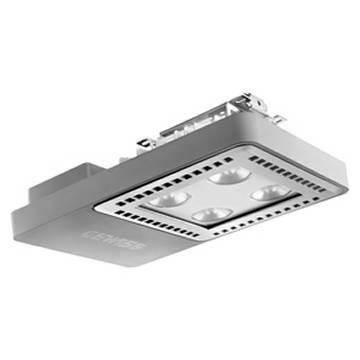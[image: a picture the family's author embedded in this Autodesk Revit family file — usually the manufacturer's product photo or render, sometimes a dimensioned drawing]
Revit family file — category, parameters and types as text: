
# Revit family: Lighting-Industrial-GEWISS-SMART[4]HE_HIGHBAYS-LED_EMERGENCY_1M
name_source: partatom
category: Apparecchi per illuminazione
units: mm (PartAtom-declared; Revit-internal decimal feet)

## family parameters
Basato su piano di lavoro = Sì
Condiviso = No
Numero OmniClass = 23.80.70.00
Punto di calcolo locali = No
Quota connettore circolare = Usa diametro
Sempre verticale = No
Sorgente d'illuminazione = No
Taglio con vuoti quando caricato = No
Tipo di parte = Normale
Titolo OmniClass = Lighting

## types (18) — shared parameters
Application = Internal
Batteria = <Per categoria>
Body = PA6 "Halogen Free" loaded fibreglass
Carico apparente = 53 VA
Catalogue = LIGHTING
Classification: = -
Classificazione = Lighting
Color Rendering Index = CRI-80
Colour = Grey RAL 7035
Colour : = Grey RAL 7035
Context = Logistics and industrial manufacturing lighting
Control System = 1 x DALI DT6 + 1 x DALI DT1 (Emerg. 3h)
DIN 18032-3 certification = -
Device with reduced surface temperature = Yes
Distanza tot_plafoniera = 74 mm  [stored 0.242782 ft]
Driver = Included
Driver Box = Built-in
Electrocod = 2444
Eletrical and lighting features = -
External screw = Stainless steel
Fixing = -
Fotometrico = GWL1093E-CL11813-16I - EME.IES
Gasket = anti-aging silicone
General information = -
Glow Wire Test : = 850 °C
IDF = 8e26bf0e-866f-493d-a6be-55b7795095e9
IDT = 99cc2ba6225c472dbcbc7a8f8b209142
IP degree = IP65
IPEA = -
Immagine tipo = GWL1093E.jpg
Installationa and maintenance = -
Insulation class = I
LED Maintenance = NiMh Battery Only
Lampada = LED
Larghezza = 253 mm  [stored 0.830052 ft]
Lifetime = L90B10 (Tq+25°C) = 100.000 h - L90B10 (Tq+50°C) = 50.000 h
Locking Hook = -
Luminaire = LED Industrial ReflectorÂ
Lunghezza = 383 mm  [stored 1.25656 ft]
Materials = -
Maximum surface exposed to the wind : = 0,140 m²
Mouting and installation = Ceiling light - Suspension
Operating temperature : = 0 ÷ +40 °C
Optic Maintenance = Non-replaceable
Optic and illuminating features = -
Overvoltage protection = DM 6 kV / CM 10 kV
Photobiological Risk Class = RG0
Plafoniera = <Per categoria>
Produttore = GEWISS S.p.A.
Prospetto di default = 1219 mm
Raggio led = 30 mm  [stored 0.0984252 ft]
Rated frequency (Hz) = 50/60 Hz
Shield type = Tempered glass Thickness 4mm
Shock resistance = IK08
Spessore plafoniera = 40 mm  [stored 0.131234 ft]
Standard Deviation Colour Matching = SDCM = 3
Standard- = EN 60598-2-22 ; EN 60598-1 ; EN 60598-2-24
Standards and approvals = -
Stocking temperature = -40 +70 °C
Supply voltage = 220 - 240 V
System power : = 48 W (+5W Emerg.)
Technical sheet = https://www.gewiss.com
Tilt- = -
Trasformatore = <Per categoria>
Type of light source = LED - Not replaceable
URL = https://www.gewiss.com
Unique digital code (Datamatrix) = Datamatrix
Version file RFA = 20.11
Vetro acceso = Lampada accesa
Voltaggio = 230 V
Warranty = 5 years
Weight (kg): = 5
Wiring = With GW connect watertight connector

## per-type parameters (varying)
| type | Colour temperature | Descrizione | Efficiency (lm/W) | Lumen output (lm) : | Modello | Optic | Optic : | Unified Glare Rating |
| GWS4124AC830 - SMART4LB 1M EMERG ASI.30K | 3000K | SMART[4]LB 1M EMERG ASI.30K | 113 | 6000 (710 Emerg.) | GWS4124AC830 | Asymmetrical | Metallic PC reflector and PMMA lenses | - |
| GWS4124AQ840 - SMART4LB 1M EMERG ELL.40K | 4000K | SMART[4]LB 1M EMERG ELL.40K | 119 | 6300 (750 Emerg.) | GWS4124AQ840 | Elliptical | Metallic PC reflector and PMMA lenses | - |
| GWS4124AA840 - SMART4LB 1M EMERG ARR.40K | 4000K | SMART[4]LB 1M EMERG ARR.40K | 134 | 7100 (850 Emerg.) | GWS4124AA840 | Array | Metallized polycarbonate reflector | - |
| GWS4124AA830 - SMART4LB 1M EMERG ARR.30K | 3000K | SMART[4]LB 1M EMERG ARR.30K | 126 | 6700 (810 Emerg.) | GWS4124AA830 | Array | Metallized polycarbonate reflector | - |
| GWS4124AP840 - SMART4LB 1M EMERG 90° 40K | 4000K | SMART[4]LB 1M EMERG 90° 40K | 136 | 7200 (850 Emerg.) | GWS4124AP840 | 90° | Metallic PC reflector and PMMA lenses | UGR - 25 |
| GWS4124AH830 - SMART4LB 1M EMERG 60° 30K | 3000K | SMART[4]LB 1M EMERG 60° 30K | 126 | 6700 (810 Emerg.) | GWS4124AH830 | 60° | Metallic PC reflector and PMMA lenses | UGR - 22 |
| GWS4124AF840 - SMART4LB 1M EMERG 30° 40K | 4000K | SMART[4]LB 1M EMERG 30° 40K | 132 | 7000 (850 Emerg.) | GWS4124AF840 | 30° | Metallic PC reflector and PMMA lenses | UGR - 22 |
| GWS4124AQ830 - SMART4LB 1M EMERG ELL.30K | 3000K | SMART[4]LB 1M EMERG ELL.30K | 113 | 6000 (710 Emerg.) | GWS4124AQ830 | Elliptical | Metallic PC reflector and PMMA lenses | - |
| GWS4124AP857 - SMART4LB 1M EMERG 90° 57K | 5700K | SMART[4]LB 1M EMERG 90° 57K | 136 | 7200 (850 Emerg.) | GWS4124AP857 | 90° | Metallic PC reflector and PMMA lenses | UGR - 25 |
| GWS4124AF857 - SMART4LB 1M EMERG 30° 57K | 5700K | SMART[4]LB 1M EMERG 30° 57K | 132 | 7000 (850 Emerg.) | GWS4124AF857 | 30° | Metallic PC reflector and PMMA lenses | UGR - 22 |
| GWS4124AH857 - SMART4LB 1M EMERG 60° 57K | 5700K | SMART[4]LB 1M EMERG 60° 57K | 132 | 7000 (850 Emerg.) | GWS4124AH857 | 60° | Metallic PC reflector and PMMA lenses | UGR - 22 |
| GWS4124AP830 - SMART4LB 1M EMERG 90° 30K | 3000K | SMART[4]LB 1M EMERG 90° 30K | 128 | 6800 (810 Emerg.) | GWS4124AP830 | 90° | Metallic PC reflector and PMMA lenses | UGR - 25 |
| GWS4124AC857 - SMART4LB 1M EMERG ASI.57K | 5700K | SMART[4]LB 1M EMERG ASI.57K | 119 | 6300 (750 Emerg.) | GWS4124AC857 | Asymmetrical | Metallic PC reflector and PMMA lenses | - |
| GWS4124AA857 - SMART4LB 1M EMERG ARR.57K | 5700K | SMART[4]LB 1M EMERG ARR.57K | 134 | 7100 (850 Emerg.) | GWS4124AA857 | Array | Metallized polycarbonate reflector | - |
| GWS4124AH840 - SMART4LB 1M EMERG 60° 40K | 4000K | SMART[4]LB 1M EMERG 60° 40K | 132 | 7000 (850 Emerg.) | GWS4124AH840 | 60° | Metallic PC reflector and PMMA lenses | UGR - 22 |
| GWS4124AC840 - SMART4LB 1M EMERG ASI.40K | 4000K | SMART[4]LB 1M EMERG ASI.40K | 119 | 6300 (750 Emerg.) | GWS4124AC840 | Asymmetrical | Metallic PC reflector and PMMA lenses | - |
| GWS4124AF830 - SMART4LB 1M EMERG 30° 30K | 3000K | SMART[4]LB 1M EMERG 30° 30K | 125 | 6600 (810 Emerg.) | GWS4124AF830 | 30° | Metallic PC reflector and PMMA lenses | UGR - 22 |
| GWS4124AQ857 - SMART4LB 1M EMERG ELL.57K | 5700K | SMART[4]LB 1M EMERG ELL.57K | 119 | 6300 (750 Emerg.) | GWS4124AQ857 | Elliptical | Metallic PC reflector and PMMA lenses | - |

note: [stored X ft] marks values corroborated as IEEE doubles in the binary element streams (Revit-internal decimal feet)

## geometry (parser evidence)
native form markers: Blend x4
no freeform markers — native parametric forms only
